# Revit family: JC KONTAKTER JCK211 Armbågskontakt
name_source: partatom
category: Specialty Equipment
units: mm (PartAtom-declared; Revit-internal decimal feet)

## family parameters
Always vertical = Yes
Cut with Voids When Loaded = No
Enable Cutting in Views = Yes
Host = Wall
Maintain Annotation Orientation = No
Part Type = Normal
Room Calculation Point = No
Round Connector Dimension = Use Diameter
Shared = No

## types (1)
- Armbågskontakt JCK211
    Antal mikrobrytare = 1
    CE Dokument = https://jckontakter.se
    Core Finish = ABS 750SW (Vit)
    Default Elevation = 0 mm  [stored 0 ft]
    Description = JCK211 är en tålig armbågskontakt med konvex tryckplatta och taktila rillor som standard. Rillorna underlättar för synsvaga att veta var de ska trycka för att aktivera armbågskontakten.
Modellen har vitt lock och vit underdel.
JCK211 levereras med 1st mikrobrytare i IP67, men går även att beställa med fler.
    Lid Finish = ABS 750SW (Vit)
    Lägsta märkström = 1mA/4 V DC
    Manufacturer = JC Kontakter
    Mikrobrytare = Standard NO IP67
    Model = JCK211
    Nominell märkström = 12 V - Resistive 6A Inductive L/R 5ms 6A, 24 V - Resistive 6A Inductive L/R 5ms 5A
    Placering av armbågskontakt = https://jckontakter.se
    Produktvikt = 0.230 kg
    Tekniskt produktblad = https://jckontakter.se
    Tillvalsförteckning = https://jckontakter.se
    Tillverkningsland = Sverige
    URL = https://jckontakter.se

note: [stored X ft] marks values corroborated as IEEE doubles in the binary element streams (Revit-internal decimal feet)

## geometry (parser evidence)
native form markers: Sweep x10
no freeform markers — native parametric forms only
